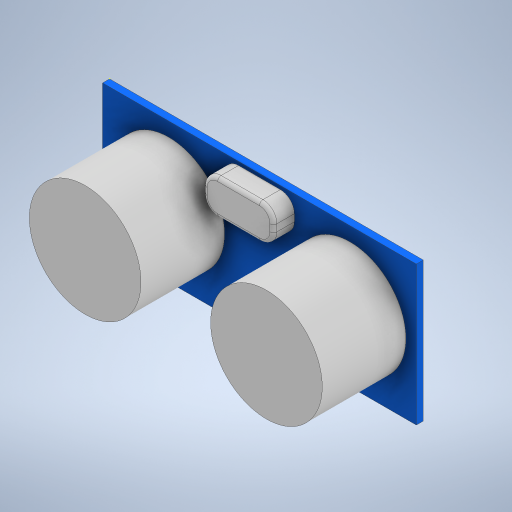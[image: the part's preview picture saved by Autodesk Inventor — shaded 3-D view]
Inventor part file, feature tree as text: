
AUTODESK INVENTOR PART (.ipt)
format: ipt  version: 2024.2 (Build 282272000, 272)  size: 330,240 bytes
history: native  units: mm
features: sketch x5, extrude x4, fillet x2
ambient origin geometry x8: Origin, YZ Plane, XZ Plane, XY Plane, X Axis, Y Axis, Z Axis, Center Point
bodies: Solid1 (feature_tree)
feature tree (11):
  extrude  "Extrusion1"  Depth=20.0mm
  extrude  "Extrusion2"  Depth=1.0mm
  extrude  "Extrusion3"  Depth=10.0mm
  fillet  "Fillet1"  Radius=10.0mm
  fillet  "Fillet2"  Radius=9.5mm
  sketch  "Sketch4"  dims[d9=12.0mm d10=0.0mm d11=10.0mm]
  extrude  "Extrusion4"  Depth=10.0mm
  sketch  "Sketch1"  dims[d0=45.0mm d1=20.0mm]
  sketch  "Sketch2"  dims[d2=1.0mm d3=0.0mm d4=16.0mm]
  sketch  "Sketch3"  dims[d5=16.0mm d6=26.0mm d7=10.0mm d8=9.5mm]
  sketch  "Sketch5"  dims[d12=5.0mm d13=17.5mm d14=0.5mm d15=3.0mm d16=0.0mm d17=2.0mm d18=0.5mm d20=10.0mm d21=17.5mm d22=10.0mm d23=0.0mm d24=0.5mm d25=2.5mm]
